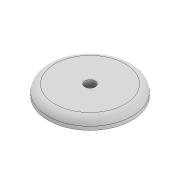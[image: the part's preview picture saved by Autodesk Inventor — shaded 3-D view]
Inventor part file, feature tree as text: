
AUTODESK INVENTOR PART (.ipt)
format: ipt  version: 2022 (Build 260153000, 153)  size: 101,888 bytes
history: native  units: mm
features: extrude x1, fillet x1, sketch x1
ambient origin geometry x8: Origin, YZ Plane, XZ Plane, XY Plane, X Axis, Y Axis, Z Axis, Center Point
bodies: Solid1 (feature_tree)
feature tree (3):
  extrude  "Extrusion1"  Depth=1.0mm
  fillet  "Fillet1"  Radius=1.5mm
  sketch  "Sketch1"  dims[d0=1.5mm d1=12.0mm d2=1.5mm d3=0.0mm d4=1.0mm]
